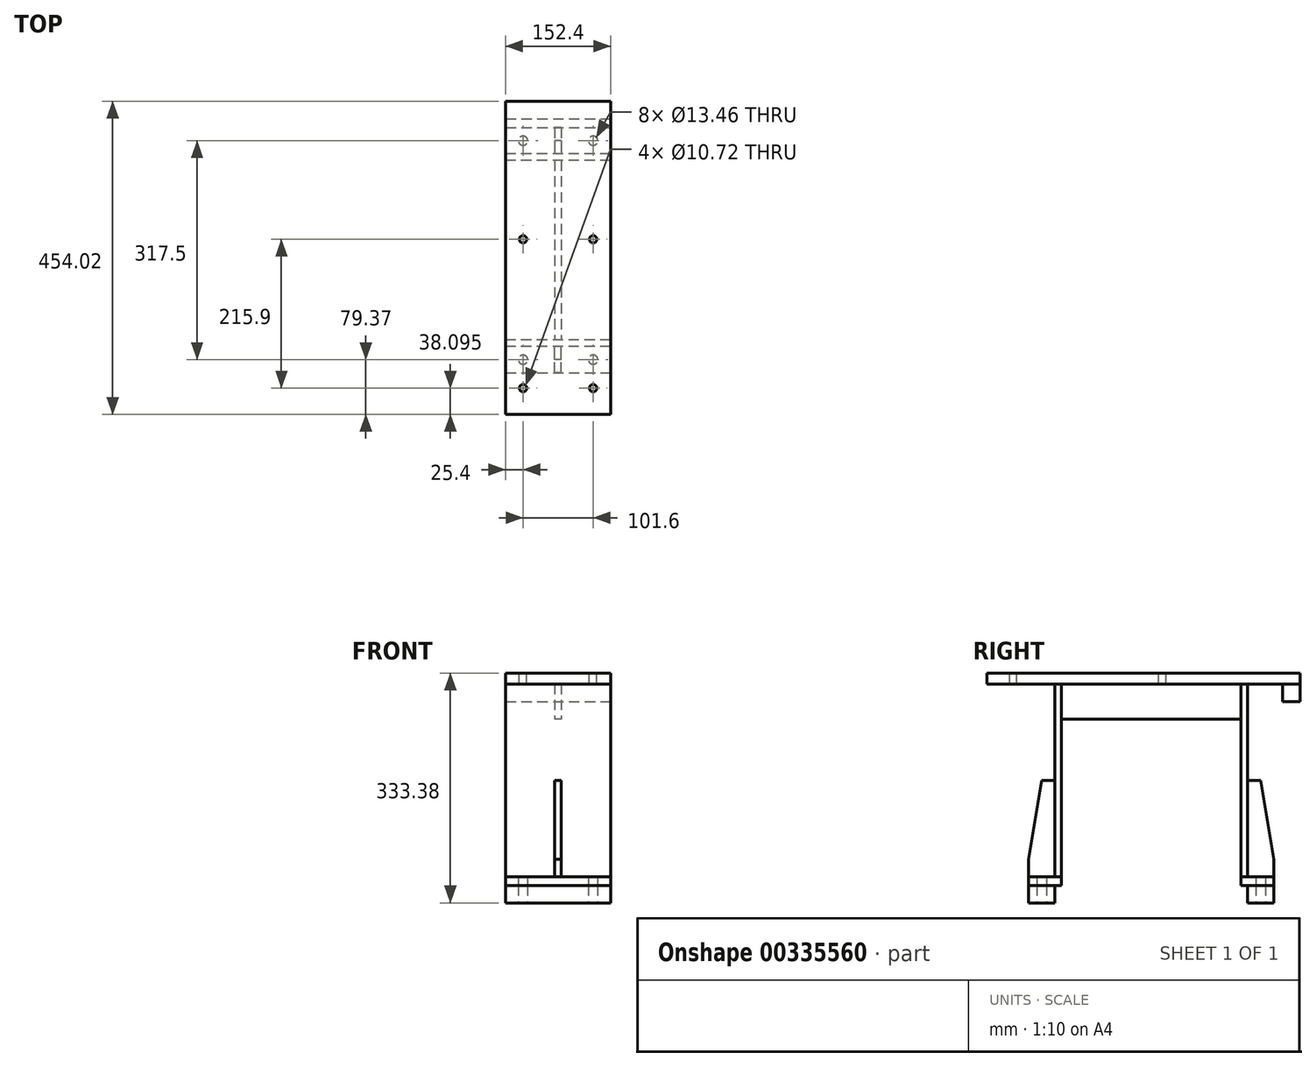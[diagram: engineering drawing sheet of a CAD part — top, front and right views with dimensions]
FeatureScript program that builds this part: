
annotation { "Feature Type Name" : "Feature", "Feature Type Description" : "" }
export const myFeature = defineFeature(function(context is Context, id is Id, definition is map)
    precondition{}
    {
        {
            var Q0;
            Q0=qCreatedBy(makeId("Top.planeOp"),FACE);
            var sketch = newSketch(context, id + "F0", { "sketchPlane" : qUnion([Q0])});
            skLineSegment(sketch, "E0.bottom", {"start": v(-127, 190.5) * mm, "end": v(127, 190.5) * mm, "construction": true});
            skLineSegment(sketch, "E0.top", {"start": v(-127, -190.5) * mm, "end": v(127, -190.5) * mm, "construction": true});
            skLineSegment(sketch, "E0.left", {"start": v(-127, 190.5) * mm, "end": v(-127, -190.5) * mm, "construction": true});
            skLineSegment(sketch, "E0.right", {"start": v(127, 190.5) * mm, "end": v(127, -190.5) * mm, "construction": true});
            skPoint(sketch, "E0.middle", {"position": v(0, 0) * mm});
            skLineSegment(sketch, "E1", {"start": v(-225.38, 0) * mm, "end": v(234.7, 0) * mm, "construction": true});
            skLineSegment(sketch, "E2", {"start": v(0, 216.86) * mm, "end": v(0, -237.52) * mm, "construction": true});
            skPoint(sketch, "E2.endSnap0", {"position": v(0, -190.5) * mm});
            skLineSegment(sketch, "E3.0", {"start": v(-225.38, -139.7) * mm, "end": v(234.7, -139.7) * mm, "construction": true});
            skLineSegment(sketch, "E4.bottom", {"start": v(-76.2, -139.7) * mm, "end": v(76.2, -139.7) * mm});
            skLineSegment(sketch, "E4.top", {"start": v(-76.2, -177.8) * mm, "end": v(76.2, -177.8) * mm});
            skLineSegment(sketch, "E4.left", {"start": v(-76.2, -139.7) * mm, "end": v(-76.2, -177.8) * mm});
            skLineSegment(sketch, "E4.right", {"start": v(76.2, -139.7) * mm, "end": v(76.2, -177.8) * mm});
            skLineSegment(sketch, "E5.MirrorCS", {"start": v(76.2, 139.7) * mm, "end": v(76.2, 177.8) * mm});
            skLineSegment(sketch, "E6.MirrorCS", {"start": v(-76.2, 139.7) * mm, "end": v(-76.2, 177.8) * mm});
            skPoint(sketch, "E7.MirrorP", {"position": v(0, 190.5) * mm});
            skLineSegment(sketch, "E8.MirrorCS", {"start": v(-76.2, 177.8) * mm, "end": v(76.2, 177.8) * mm});
            skLineSegment(sketch, "E9.MirrorCS", {"start": v(-76.2, 139.7) * mm, "end": v(76.2, 139.7) * mm});
            skLineSegment(sketch, "E10", {"start": v(76.2, -158.75) * mm, "end": v(-76.2, -158.75) * mm, "construction": true});
            skLineSegment(sketch, "E11.0", {"start": v(-50.8, 216.86) * mm, "end": v(-50.8, -237.52) * mm, "construction": true});
            skLineSegment(sketch, "E12.MirrorCS", {"start": v(50.8, 216.86) * mm, "end": v(50.8, -237.52) * mm, "construction": true});
            skCircle(sketch, "E13", {"center": v(-50.8, -158.75) * mm, "radius": 6.73 * mm});
            skCircle(sketch, "E14", {"center": v(50.8, -158.75) * mm, "radius": 6.73 * mm});
            skCircle(sketch, "E15.MirrorC", {"center": v(-50.8, 158.75) * mm, "radius": 6.73 * mm});
            skCircle(sketch, "E16.MirrorC", {"center": v(50.8, 158.75) * mm, "radius": 6.73 * mm});
            skSolve(sketch);
        }
        {
            var Q0;
            Q0=qSketchRegion(id+"F0",true);
            extrude(context, id + "F1", {"entities" : qUnion([Q0]), "depth" : 25.4 * mm});
        }
        {
            var Q0;
            Q0=makeQuery(id+"F1.opExtrude","CAP_FACE",FACE,{"disambiguationData":[OSD([sQuery(id+"F0.wireOp",EDGE,"E4.bottom"),sQuery(id+"F0.wireOp",EDGE,"E4.top"),sQuery(id+"F0.wireOp",EDGE,"E4.left"),sQuery(id+"F0.wireOp",EDGE,"E4.right"),sQuery(id+"F0.wireOp",EDGE,"E13"),sQuery(id+"F0.wireOp",EDGE,"E14")])],"isStart":false});
            var sketch = newSketch(context, id + "F2", { "sketchPlane" : qUnion([Q0])});
            skLineSegment(sketch, "E17.0.0", {"start": v(-76.2, -130.18) * mm, "end": v(-76.2, -177.8) * mm});
            skLineSegment(sketch, "E17.0.1", {"start": v(-76.2, -177.8) * mm, "end": v(76.2, -177.8) * mm});
            skLineSegment(sketch, "E17.0.2", {"start": v(76.2, -177.8) * mm, "end": v(76.2, -130.18) * mm});
            skCircle(sketch, "E18.0", {"center": v(-50.8, -158.75) * mm, "radius": 6.73 * mm});
            skCircle(sketch, "E19.0", {"center": v(50.8, -158.75) * mm, "radius": 6.73 * mm});
            skLineSegment(sketch, "E20.0", {"start": v(76.2, -130.18) * mm, "end": v(-76.2, -130.18) * mm});
            skPoint(sketch, "E21.orphan", {"position": v(-76.2, -139.7) * mm});
            skPoint(sketch, "E22.orphan", {"position": v(76.2, -139.7) * mm});
            skSolve(sketch);
        }
        {
            var Q0;
            Q0=qSketchRegion(id+"F2",true);
            extrude(context, id + "F3", {"entities" : qUnion([Q0]), "depth" : 12.7 * mm});
        }
        {
            var Q0;
            Q0=makeQuery(id+"F3.opExtrude","CAP_FACE",FACE,{"disambiguationData":[OSD([sQuery(id+"F2.wireOp",EDGE,"E17.0.0"),sQuery(id+"F2.wireOp",EDGE,"E17.0.1"),sQuery(id+"F2.wireOp",EDGE,"E17.0.2"),sQuery(id+"F2.wireOp",EDGE,"E18.0"),sQuery(id+"F2.wireOp",EDGE,"E19.0"),sQuery(id+"F2.wireOp",EDGE,"E20.0")])],"isStart":false});
            var sketch = newSketch(context, id + "F4", { "sketchPlane" : qUnion([Q0])});
            skLineSegment(sketch, "E23.0", {"start": v(76.2, -130.18) * mm, "end": v(-76.2, -130.18) * mm});
            skLineSegment(sketch, "E24.0", {"start": v(76.2, -139.7) * mm, "end": v(-76.2, -139.7) * mm});
            skLineSegment(sketch, "E25", {"start": v(-76.2, -139.7) * mm, "end": v(-76.2, -130.18) * mm});
            skLineSegment(sketch, "E26", {"start": v(76.2, -130.18) * mm, "end": v(76.2, -139.7) * mm});
            skSolve(sketch);
        }
        {
            var Q0;
            Q0=qSketchRegion(id+"F4",true);
            extrude(context, id + "F5", {"entities" : qUnion([Q0]), "depth" : 279.4 * mm});
        }
        {
            var Q0;
            Q0=makeQuery(id+"F3.opExtrude","SWEPT_BODY",BODY,{"disambiguationData":[OSD([sQuery(id+"F2.wireOp",EDGE,"E17.0.0"),sQuery(id+"F2.wireOp",EDGE,"E17.0.1"),sQuery(id+"F2.wireOp",EDGE,"E17.0.2"),sQuery(id+"F2.wireOp",EDGE,"E18.0"),sQuery(id+"F2.wireOp",EDGE,"E19.0"),sQuery(id+"F2.wireOp",EDGE,"E20.0")])]});
            var Q1;
            Q1=makeQuery(id+"F5.opExtrude","SWEPT_BODY",BODY,{"disambiguationData":[OSD([sQuery(id+"F4.wireOp",EDGE,"E23.0"),sQuery(id+"F4.wireOp",EDGE,"E24.0"),sQuery(id+"F4.wireOp",EDGE,"E25"),sQuery(id+"F4.wireOp",EDGE,"E26")])]});
            var Q2;
            Q2=qCreatedBy(makeId("Front.planeOp"),FACE);
            mirror(context, id + "F6", {"entities" : qUnion([Q0, Q1]), "mirrorPlane" : qUnion([Q2])});
        }
        {
            var Q0;
            Q0=makeQuery(id+"F5.opExtrude","CAP_FACE",FACE,{"disambiguationData":[OSD([sQuery(id+"F4.wireOp",EDGE,"E23.0"),sQuery(id+"F4.wireOp",EDGE,"E24.0"),sQuery(id+"F4.wireOp",EDGE,"E25"),sQuery(id+"F4.wireOp",EDGE,"E26")])],"isStart":false});
            var sketch = newSketch(context, id + "F7", { "sketchPlane" : qUnion([Q0])});
            skLineSegment(sketch, "E27", {"start": v(141.16, 0) * mm, "end": v(-134.92, 0) * mm, "construction": true});
            skLineSegment(sketch, "E28.0", {"start": v(141.16, 215.9) * mm, "end": v(-134.92, 215.9) * mm, "construction": true});
            skLineSegment(sketch, "E29.0", {"start": v(141.16, -238.13) * mm, "end": v(-134.92, -238.13) * mm, "construction": true});
            skLineSegment(sketch, "E30.0", {"start": v(76.2, 215.9) * mm, "end": v(76.2, -238.13) * mm, "construction": true});
            skPoint(sketch, "E31.orphan", {"position": v(76.2, 177.8) * mm});
            skPoint(sketch, "E32.orphan", {"position": v(76.2, 130.18) * mm});
            skLineSegment(sketch, "E33.bottom", {"start": v(76.2, 215.9) * mm, "end": v(-76.2, 215.9) * mm});
            skLineSegment(sketch, "E33.top", {"start": v(76.2, -238.13) * mm, "end": v(-76.2, -238.13) * mm});
            skLineSegment(sketch, "E33.left", {"start": v(76.2, 215.9) * mm, "end": v(76.2, -238.13) * mm});
            skLineSegment(sketch, "E33.right", {"start": v(-76.2, 215.9) * mm, "end": v(-76.2, -238.13) * mm});
            skSolve(sketch);
        }
        {
            var Q0;
            Q0=qSketchRegion(id+"F7",true);
            extrude(context, id + "F8", {"entities" : qUnion([Q0]), "depth" : 15.88 * mm});
        }
        {
            var Q0;
            Q0=makeQuery(id+"F8.opExtrude","CAP_FACE",FACE,{"disambiguationData":[OSD([sQuery(id+"F7.wireOp",EDGE,"E33.bottom"),sQuery(id+"F7.wireOp",EDGE,"E33.top"),sQuery(id+"F7.wireOp",EDGE,"E33.left"),sQuery(id+"F7.wireOp",EDGE,"E33.right")])],"isStart":true});
            var sketch = newSketch(context, id + "F9", { "sketchPlane" : qUnion([Q0])});
            skLineSegment(sketch, "E34.0", {"start": v(76.2, -215.9) * mm, "end": v(-76.2, -215.9) * mm, "construction": true});
            skLineSegment(sketch, "E35.bottom", {"start": v(-76.2, -215.9) * mm, "end": v(76.2, -215.9) * mm});
            skLineSegment(sketch, "E35.top", {"start": v(-76.2, -190.5) * mm, "end": v(76.2, -190.5) * mm});
            skLineSegment(sketch, "E35.left", {"start": v(-76.2, -215.9) * mm, "end": v(-76.2, -190.5) * mm});
            skLineSegment(sketch, "E35.right", {"start": v(76.2, -215.9) * mm, "end": v(76.2, -190.5) * mm});
            skSolve(sketch);
        }
        {
            var Q0;
            Q0=qSketchRegion(id+"F9",true);
            extrude(context, id + "F10", {"entities" : qUnion([Q0]), "depth" : 25.4 * mm});
        }
        {
            var Q0;
            Q0=qCreatedBy(makeId("Right.planeOp"),FACE);
            var sketch = newSketch(context, id + "F11", { "sketchPlane" : qUnion([Q0])});
            skLineSegment(sketch, "E36.0", {"start": v(130.18, 317.5) * mm, "end": v(-130.17, 317.5) * mm, "construction": true});
            skLineSegment(sketch, "E37.0.1", {"start": v(130.18, 38.1) * mm, "end": v(130.18, 317.5) * mm, "construction": true});
            skLineSegment(sketch, "E37.0.3", {"start": v(130.18, 317.5) * mm, "end": v(130.18, 38.1) * mm, "construction": true});
            skLineSegment(sketch, "E38.0.1", {"start": v(-130.18, 38.1) * mm, "end": v(-130.18, 317.5) * mm, "construction": true});
            skLineSegment(sketch, "E38.0.3", {"start": v(-130.18, 317.5) * mm, "end": v(-130.18, 38.1) * mm, "construction": true});
            skPoint(sketch, "E39.orphan", {"position": v(-238.13, 317.5) * mm});
            skPoint(sketch, "E40.orphan", {"position": v(215.9, 317.5) * mm});
            skLineSegment(sketch, "E41.bottom", {"start": v(130.18, 317.5) * mm, "end": v(-130.18, 317.5) * mm});
            skLineSegment(sketch, "E41.top", {"start": v(130.18, 266.7) * mm, "end": v(-130.18, 266.7) * mm});
            skLineSegment(sketch, "E41.left", {"start": v(130.18, 317.5) * mm, "end": v(130.18, 266.7) * mm});
            skLineSegment(sketch, "E41.right", {"start": v(-130.18, 317.5) * mm, "end": v(-130.18, 266.7) * mm});
            skSolve(sketch);
        }
        {
            var Q0;
            Q0=makeQuery(id+"F11.imprint","IMPRINT",FACE,{"disambiguationData":[TD([[makeQuery(id+"F11.imprint","IMPRINT",EDGE,{"derivedFrom":sQuery(id+"F11.wireOp",EDGE,"E41.bottom")}),1.0]])]});
            extrude(context, id + "F12", {"entities" : qUnion([Q0]), "endBound" : BoundingType.SYMMETRIC, "depth" : 9.52 * mm});
        }
        {
            var Q0;
            Q0=makeQuery(id+"F5.opExtrude","SWEPT_FACE",FACE,{"disambiguationData":[OSD([sQuery(id+"F4.wireOp",EDGE,"E24.0")])]});
            var sketch = newSketch(context, id + "F13", { "sketchPlane" : qUnion([Q0])});
            skLineSegment(sketch, "E42.0", {"start": v(76.2, 38.1) * mm, "end": v(-76.2, 38.1) * mm, "construction": true});
            skLineSegment(sketch, "E43", {"start": v(0, -119.88) * mm, "end": v(0, 176.84) * mm, "construction": true});
            skLineSegment(sketch, "E44.0", {"start": v(4.76, -119.88) * mm, "end": v(4.76, 176.84) * mm, "construction": true});
            skLineSegment(sketch, "E45.bottom", {"start": v(4.76, 38.1) * mm, "end": v(-4.76, 38.1) * mm});
            skLineSegment(sketch, "E45.top", {"start": v(4.76, 177.8) * mm, "end": v(-4.76, 177.8) * mm});
            skLineSegment(sketch, "E45.left", {"start": v(4.76, 38.1) * mm, "end": v(4.76, 177.8) * mm});
            skLineSegment(sketch, "E45.right", {"start": v(-4.76, 38.1) * mm, "end": v(-4.76, 177.8) * mm});
            skSolve(sketch);
        }
        {
            var Q0;
            Q0=qSketchRegion(id+"F13",true);
            extrude(context, id + "F14", {"entities" : qUnion([Q0]), "depth" : 38.1 * mm});
        }
        {
            var Q0;
            Q0=makeQuery(id+"F14.opExtrude","SWEPT_FACE",FACE,{"disambiguationData":[OSD([sQuery(id+"F13.wireOp",EDGE,"E45.right")])]});
            var sketch = newSketch(context, id + "F15", { "sketchPlane" : qUnion([Q0])});
            skLineSegment(sketch, "E46.0", {"start": v(130.18, 63.5) * mm, "end": v(177.8, 63.5) * mm, "construction": true});
            skLineSegment(sketch, "E47", {"start": v(177.8, 63.5) * mm, "end": v(158.75, 177.8) * mm});
            skLineSegment(sketch, "E48", {"start": v(158.75, 177.8) * mm, "end": v(177.8, 177.8) * mm});
            skLineSegment(sketch, "E49", {"start": v(177.8, 177.8) * mm, "end": v(177.8, 63.5) * mm});
            skSolve(sketch);
        }
        {
            var Q0;
            Q0=qSketchRegion(id+"F15",true);
            extrude(context, id + "F16", {"entities" : qUnion([Q0]), "operationType" : NewBodyOperationType.REMOVE, "endBound" : BoundingType.THROUGH_ALL, "oppositeDirection" : true, "depth" : 25.4 * mm});
        }
        {
            var Q0;
            Q0=makeQuery(id+"F14.opExtrude","SWEPT_BODY",BODY,{"disambiguationData":[OSD([sQuery(id+"F13.wireOp",EDGE,"E45.bottom"),sQuery(id+"F13.wireOp",EDGE,"E45.top"),sQuery(id+"F13.wireOp",EDGE,"E45.left"),sQuery(id+"F13.wireOp",EDGE,"E45.right")])]});
            var Q1;
            Q1=qCreatedBy(makeId("Front.planeOp"),FACE);
            mirror(context, id + "F17", {"entities" : qUnion([Q0]), "mirrorPlane" : qUnion([Q1])});
        }
        {
            var Q0;
            Q0=makeQuery(id+"F8.opExtrude","CAP_FACE",FACE,{"disambiguationData":[OSD([sQuery(id+"F7.wireOp",EDGE,"E33.bottom"),sQuery(id+"F7.wireOp",EDGE,"E33.top"),sQuery(id+"F7.wireOp",EDGE,"E33.left"),sQuery(id+"F7.wireOp",EDGE,"E33.right")])],"isStart":false});
            var sketch = newSketch(context, id + "F18", { "sketchPlane" : qUnion([Q0])});
            skLineSegment(sketch, "E50.0", {"start": v(76.2, 215.9) * mm, "end": v(-76.2, 215.9) * mm, "construction": true});
            skLineSegment(sketch, "E51.0", {"start": v(76.2, 15.87) * mm, "end": v(-76.2, 15.87) * mm, "construction": true});
            skLineSegment(sketch, "E52.0", {"start": v(76.2, -200.03) * mm, "end": v(-76.2, -200.03) * mm, "construction": true});
            skLineSegment(sketch, "E53", {"start": v(0, 215.9) * mm, "end": v(0, -279.2) * mm, "construction": true});
            skLineSegment(sketch, "E54.0", {"start": v(-50.8, 215.9) * mm, "end": v(-50.8, -279.2) * mm, "construction": true});
            skPoint(sketch, "E55", {"position": v(-50.8, 15.87) * mm});
            skPoint(sketch, "E56", {"position": v(-50.8, -200.03) * mm});
            skPoint(sketch, "E57.MirrorP", {"position": v(50.8, 15.87) * mm});
            skPoint(sketch, "E58.MirrorP", {"position": v(50.8, -200.03) * mm});
            skSolve(sketch);
        }
        {
            var Q0;
            Q0=sQuery(id+"F18.wireOp",VERTEX,"E57.MirrorP");
            var Q1;
            Q1=sQuery(id+"F18.wireOp",VERTEX,"E55");
            var Q2;
            Q2=sQuery(id+"F18.wireOp",VERTEX,"E58.MirrorP");
            var Q3;
            Q3=sQuery(id+"F18.wireOp",VERTEX,"E56");
            var Q4;
            Q4=makeQuery(id+"F8.opExtrude","SWEPT_BODY",BODY,{"disambiguationData":[OSD([sQuery(id+"F7.wireOp",EDGE,"E33.bottom"),sQuery(id+"F7.wireOp",EDGE,"E33.top"),sQuery(id+"F7.wireOp",EDGE,"E33.left"),sQuery(id+"F7.wireOp",EDGE,"E33.right")])]});
            hole(context, id + "F19", {"style" : HoleStyle.SIMPLE, "endStyle" : HoleEndStyle.BLIND, "standardTappedOrClearance" : lookupTablePath({ "standard" : "ANSI", "engagement" : "75%", "pitch" : "13 tpi", "size" : "1/2", "type" : "Tapped" }), "standardBlindInLast" : lookupTablePath({ "standard" : "ANSI", "engagement" : "75%", "pitch" : "13 tpi", "size" : "1/2", "type" : "Tapped" }), "holeDiameter" : 10.72 * mm, "showTappedDepth" : true, "holeDepth" : 25.4 * mm, "tappedDepth" : 19.53 * mm, "tapClearance" : 3, "locations" : qUnion([Q0, Q1, Q2, Q3]), "scope" : qUnion([Q4]), "majorDiameter" : 12.7 * mm});
        }
    });
